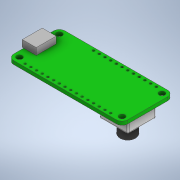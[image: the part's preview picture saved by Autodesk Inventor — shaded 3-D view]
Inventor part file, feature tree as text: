
AUTODESK INVENTOR PART (.ipt)
format: ipt  version: 2021 (Build 250183000, 183)  size: 254,464 bytes
history: native  units: in
note: dims shown in document units (in); Inventor stores cm internally (conversion verified against a paired STEP export)
features: extrude x8, sketch x8, pattern_linear x2, fillet x1, projected_geometry x1
ambient origin geometry x8: Origin, YZ Plane, XZ Plane, XY Plane, X Axis, Y Axis, Z Axis, Center Point
bodies: Solid1 (feature_tree)
feature tree (20):
  extrude  "Extrusion1"  Depth=0.9in
  extrude  "Extrusion4"  Depth=0.7in
  extrude  "Extrusion6"  Depth=0.1in
  pattern_linear  "Rectangular Pattern1"  Spacing1=0.025in  [1 undecoded]
  extrude  "Extrusion7"  Depth=0.245in
  pattern_linear  "Rectangular Pattern2"  Spacing1=0.1181in  [1 undecoded]
  extrude  "Extrusion8"  Depth=0.025in
  extrude  "Extrusion9"  Depth=0.05in
  fillet  "Fillet2"  Radius=0.05in
  extrude  "Extrusion10"  TaperAngle=0.0deg  [1 undecoded]
  extrude  "Extrusion11"  Depth=0.1in
  sketch  "Sketch1"  dims[d0=2.0in d1=0.9in]
  sketch  "Sketch4"  dims[d2=0.1in d6=0.7in]
  sketch  "Sketch6"  dims[d9=0.35in d10=0.1in]
  sketch  "Sketch7"  dims[d11=0.1in]
  sketch  "Sketch8"  dims[d13=0.1in]
  sketch  "Sketch9"  dims[d14=0.1in]
  sketch  "Sketch10"  dims[d15=0.1in]
  sketch  "Sketch11"  dims[d16=0.063in d17=0.0in d34=0.025in d35=0.245in d38=0.1181in d39=0.0in d46=0.0394in d47=0.05in d48=0.05in d49=0.0in d50=0.0in d51=6.2992in d53=0.1in d54=1.15in d55=0.05in d56=0.0394in d57=0.0in d58=0.0in d59=4.7244in d61=0.1in d62=0.35in d63=0.5in d64=1.65in d65=0.2638in d66=0.0in d67=0.28in d69=0.25in d70=0.0in d71=0.025in d72=0.32in d74=0.525in d75=0.1181in d76=0.0in d77=0.1in d78=0.025in d79=0.0in]
  projected_geometry  "Project Cut Edges1"
note: 3 required parameter values undecoded (feature->parameter linkage not recoverable at this tier; creation-order binding heuristic only, values carry confidence <= 0.55)
